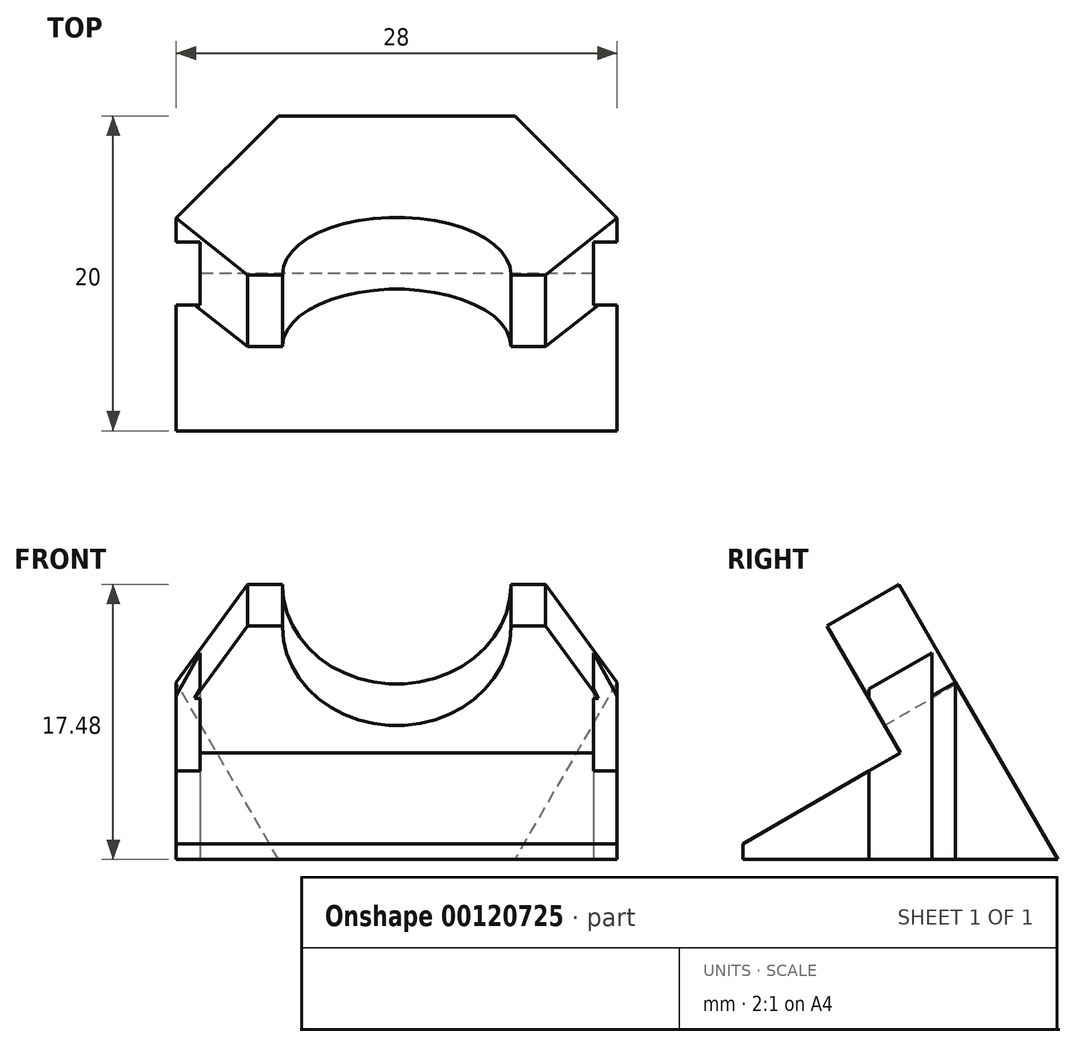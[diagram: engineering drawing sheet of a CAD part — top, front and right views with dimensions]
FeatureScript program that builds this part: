
annotation { "Feature Type Name" : "Feature", "Feature Type Description" : "" }
export const myFeature = defineFeature(function(context is Context, id is Id, definition is map)
    precondition{}
    {
        {
            var Q0;
            Q0=qCreatedBy(makeId("Top.planeOp"),FACE);
            var sketch = newSketch(context, id + "F0", { "sketchPlane" : qUnion([Q0])});
            skLineSegment(sketch, "E0.bottom", {"start": v(-14, 10) * mm, "end": v(14, 10) * mm});
            skLineSegment(sketch, "E0.top", {"start": v(-14, -10) * mm, "end": v(14, -10) * mm});
            skLineSegment(sketch, "E0.left", {"start": v(-14, 10) * mm, "end": v(-14, -10) * mm});
            skLineSegment(sketch, "E0.right", {"start": v(14, 10) * mm, "end": v(14, -10) * mm});
            skSolve(sketch);
        }
        {
            var Q0;
            Q0=makeQuery(id+"F0.imprint","IMPRINT",FACE,{"disambiguationData":[TD([[makeQuery(id+"F0.imprint","IMPRINT",EDGE,{"derivedFrom":sQuery(id+"F0.wireOp",EDGE,"E0.bottom")}),-1.0]])]});
            extrude(context, id + "F1", {"entities" : qUnion([Q0]), "depth" : 20 * mm});
        }
        {
            var Q0;
            Q0=qCreatedBy(makeId("Top.planeOp"),FACE);
            var sketch = newSketch(context, id + "F2", { "sketchPlane" : qUnion([Q0])});
            skLineSegment(sketch, "E1", {"start": v(-7.5, 10) * mm, "end": v(-14, 3.5) * mm});
            skLineSegment(sketch, "E2", {"start": v(-14, 3.5) * mm, "end": v(-14, 10) * mm});
            skLineSegment(sketch, "E3", {"start": v(-14, 10) * mm, "end": v(-7.5, 10) * mm});
            skSolve(sketch);
        }
        {
            var Q0;
            Q0 = qSketchRegion(id + "F2", true);
            extrude(context, id + "F3", {"entities" : qUnion([Q0]), "depth" : 20 * mm});
        }
        {
            var Q0;
            Q0=makeQuery(id+"F3.opExtrude","SWEPT_BODY",BODY,{"disambiguationData":[OSD([sQuery(id+"F2.wireOp",EDGE,"E1"),sQuery(id+"F2.wireOp",EDGE,"E2"),sQuery(id+"F2.wireOp",EDGE,"E3")])]});
            var Q1;
            Q1=qCreatedBy(makeId("Right.planeOp"),FACE);
            mirror(context, id + "F4", {"entities" : qUnion([Q0]), "mirrorPlane" : qUnion([Q1])});
        }
        {
            var Q0;
            Q0=qCreatedBy(makeId("Right.planeOp"),FACE);
            var sketch = newSketch(context, id + "F5", { "sketchPlane" : qUnion([Q0])});
            skLineSegment(sketch, "E4", {"start": v(10, 0) * mm, "end": v(10, 25.53) * mm});
            skLineSegment(sketch, "E5", {"start": v(10, 25.53) * mm, "end": v(-4.74, 25.53) * mm});
            skLineSegment(sketch, "E6", {"start": v(-4.74, 25.53) * mm, "end": v(10, 0) * mm});
            skSolve(sketch);
        }
        {
            var Q0;
            Q0 = qSketchRegion(id + "F5", true);
            extrude(context, id + "F6", {"entities" : qUnion([Q0]), "endBound" : BoundingType.SYMMETRIC, "depth" : 35 * mm});
        }
        {
            var Q0;
            Q0=qCreatedBy(makeId("Top.planeOp"),FACE);
            var sketch = newSketch(context, id + "F7", { "sketchPlane" : qUnion([Q0])});
            skLineSegment(sketch, "E7.bottom", {"start": v(-14, -2) * mm, "end": v(-12.5, -2) * mm});
            skLineSegment(sketch, "E7.top", {"start": v(-14, 2) * mm, "end": v(-12.5, 2) * mm});
            skLineSegment(sketch, "E7.left", {"start": v(-14, -2) * mm, "end": v(-14, 2) * mm});
            skLineSegment(sketch, "E7.right", {"start": v(-12.5, -2) * mm, "end": v(-12.5, 2) * mm});
            skSolve(sketch);
        }
        {
            var Q0;
            Q0 = qSketchRegion(id + "F7", true);
            extrude(context, id + "F8", {"entities" : qUnion([Q0]), "depth" : 40 * mm});
        }
        {
            var Q0;
            Q0=makeQuery(id+"F8.opExtrude","SWEPT_BODY",BODY,{"disambiguationData":[OSD([sQuery(id+"F7.wireOp",EDGE,"E7.bottom"),sQuery(id+"F7.wireOp",EDGE,"E7.top"),sQuery(id+"F7.wireOp",EDGE,"E7.left"),sQuery(id+"F7.wireOp",EDGE,"E7.right")])]});
            var Q1;
            Q1=qCreatedBy(makeId("Right.planeOp"),FACE);
            mirror(context, id + "F9", {"entities" : qUnion([Q0]), "mirrorPlane" : qUnion([Q1])});
        }
        {
            var Q0;
            Q0=makeQuery(id+"F3.opExtrude","SWEPT_BODY",BODY,{"disambiguationData":[OSD([sQuery(id+"F2.wireOp",EDGE,"E1"),sQuery(id+"F2.wireOp",EDGE,"E2"),sQuery(id+"F2.wireOp",EDGE,"E3")])]});
            var Q1;
            Q1=makeQuery(id+"F4.opPattern","COPY",BODY,{"derivedFrom":makeQuery(id+"F3.opExtrude","SWEPT_BODY",BODY,{"disambiguationData":[OSD([sQuery(id+"F2.wireOp",EDGE,"E1"),sQuery(id+"F2.wireOp",EDGE,"E2"),sQuery(id+"F2.wireOp",EDGE,"E3")])]}),"instanceName":"1"});
            var Q2;
            Q2=makeQuery(id+"F6.opExtrude","SWEPT_BODY",BODY,{"disambiguationData":[OSD([sQuery(id+"F5.wireOp",EDGE,"E4"),sQuery(id+"F5.wireOp",EDGE,"E5"),sQuery(id+"F5.wireOp",EDGE,"E6")])]});
            var Q3;
            Q3=makeQuery(id+"F8.opExtrude","SWEPT_BODY",BODY,{"disambiguationData":[OSD([sQuery(id+"F7.wireOp",EDGE,"E7.bottom"),sQuery(id+"F7.wireOp",EDGE,"E7.top"),sQuery(id+"F7.wireOp",EDGE,"E7.left"),sQuery(id+"F7.wireOp",EDGE,"E7.right")])]});
            var Q4;
            Q4=makeQuery(id+"F9.opPattern","COPY",BODY,{"derivedFrom":makeQuery(id+"F8.opExtrude","SWEPT_BODY",BODY,{"disambiguationData":[OSD([sQuery(id+"F7.wireOp",EDGE,"E7.bottom"),sQuery(id+"F7.wireOp",EDGE,"E7.top"),sQuery(id+"F7.wireOp",EDGE,"E7.left"),sQuery(id+"F7.wireOp",EDGE,"E7.right")])]}),"instanceName":"1"});
            var Q5;
            Q5=makeQuery(id+"F1.opExtrude","SWEPT_BODY",BODY,{"disambiguationData":[OSD([sQuery(id+"F0.wireOp",EDGE,"E0.bottom"),sQuery(id+"F0.wireOp",EDGE,"E0.top"),sQuery(id+"F0.wireOp",EDGE,"E0.left"),sQuery(id+"F0.wireOp",EDGE,"E0.right")])]});
            booleanBodies(context, id + "F10", {"operationType" : BooleanOperationType.SUBTRACTION, "tools" : qUnion([Q0, Q1, Q2, Q3, Q4]), "targets" : qUnion([Q5])});
        }
        {
            var Q0;
            Q0=qCreatedBy(makeId("Right.planeOp"),FACE);
            var sketch = newSketch(context, id + "F11", { "sketchPlane" : qUnion([Q0])});
            skLineSegment(sketch, "E8", {"start": v(-10, 1) * mm, "end": v(0, 6.77) * mm});
            skLineSegment(sketch, "E9", {"start": v(0, 6.77) * mm, "end": v(-10, 24.1) * mm});
            skLineSegment(sketch, "E10", {"start": v(-10, 24.1) * mm, "end": v(-10, 1) * mm});
            skSolve(sketch);
        }
        {
            var Q0;
            Q0=makeQuery(id+"F11.imprint","IMPRINT",FACE,{"disambiguationData":[TD([[makeQuery(id+"F11.imprint","IMPRINT",EDGE,{"derivedFrom":sQuery(id+"F11.wireOp",EDGE,"E8")}),1.0]])]});
            extrude(context, id + "F12", {"entities" : qUnion([Q0]), "endBound" : BoundingType.SYMMETRIC, "depth" : 30 * mm});
        }
        {
            var Q0;
            Q0=makeQuery(id+"F12.opExtrude","SWEPT_BODY",BODY,{"disambiguationData":[OSD([sQuery(id+"F11.wireOp",EDGE,"E8"),sQuery(id+"F11.wireOp",EDGE,"E9"),sQuery(id+"F11.wireOp",EDGE,"E10")])]});
            var Q1;
            Q1=makeQuery(id+"F1.opExtrude","SWEPT_BODY",BODY,{"disambiguationData":[OSD([sQuery(id+"F0.wireOp",EDGE,"E0.bottom"),sQuery(id+"F0.wireOp",EDGE,"E0.top"),sQuery(id+"F0.wireOp",EDGE,"E0.left"),sQuery(id+"F0.wireOp",EDGE,"E0.right")])]});
            booleanBodies(context, id + "F13", {"operationType" : BooleanOperationType.SUBTRACTION, "tools" : qUnion([Q0]), "targets" : qUnion([Q1])});
        }
        {
            var Q0;
            Q0=makeQuery(id+"F13.opBoolean","COPY",FACE,{"derivedFrom":makeQuery(id+"F12.opExtrude","SWEPT_FACE",FACE,{"disambiguationData":[OSD([sQuery(id+"F11.wireOp",EDGE,"E9")])]})});
            var sketch = newSketch(context, id + "F14", { "sketchPlane" : qUnion([Q0])});
            skLineSegment(sketch, "E11.bottom", {"start": v(0, 5.87) * mm, "end": v(9.74, 5.87) * mm});
            skLineSegment(sketch, "E11.top", {"start": v(0, 15.12) * mm, "end": v(9.74, 15.12) * mm});
            skLineSegment(sketch, "E11.left", {"start": v(0, 5.87) * mm, "end": v(0, 15.12) * mm});
            skLineSegment(sketch, "E11.right", {"start": v(9.74, 5.87) * mm, "end": v(9.74, 15.12) * mm});
            skSolve(sketch);
        }
        {
            var Q0;
            Q0=sQuery(id+"F14.wireOp",VERTEX,"E11.left.end");
            var Q1;
            Q1=makeQuery(id+"F1.opExtrude","SWEPT_BODY",BODY,{"disambiguationData":[OSD([sQuery(id+"F0.wireOp",EDGE,"E0.bottom"),sQuery(id+"F0.wireOp",EDGE,"E0.top"),sQuery(id+"F0.wireOp",EDGE,"E0.left"),sQuery(id+"F0.wireOp",EDGE,"E0.right")])]});
            hole(context, id + "F15", {"style" : HoleStyle.SIMPLE, "endStyle" : HoleEndStyle.THROUGH, "holeDiameter" : 14.5 * mm, "locations" : qUnion([Q0]), "scope" : qUnion([Q1]), "isTappedThrough" : true});
        }
        {
            var Q0;
            Q0=qCreatedBy(makeId("Right.planeOp"),FACE);
            var sketch = newSketch(context, id + "F16", { "sketchPlane" : qUnion([Q0])});
            skLineSegment(sketch, "E12", {"start": v(6, 21) * mm, "end": v(-7.5, 13.2) * mm});
            skLineSegment(sketch, "E13", {"start": v(-7.5, 13.2) * mm, "end": v(-12, 21) * mm});
            skLineSegment(sketch, "E14", {"start": v(-12, 21) * mm, "end": v(6, 21) * mm});
            skSolve(sketch);
        }
        {
            var Q0;
            Q0 = qSketchRegion(id + "F16", true);
            extrude(context, id + "F17", {"entities" : qUnion([Q0]), "endBound" : BoundingType.SYMMETRIC, "depth" : 40 * mm});
        }
        {
            var Q0;
            Q0=makeQuery(id+"F10.opBoolean","COPY",FACE,{"derivedFrom":makeQuery(id+"F6.opExtrude","SWEPT_FACE",FACE,{"disambiguationData":[OSD([sQuery(id+"F5.wireOp",EDGE,"E6")])]})});
            var sketch = newSketch(context, id + "F18", { "sketchPlane" : qUnion([Q0])});
            skLineSegment(sketch, "E15", {"start": v(8, 17.5) * mm, "end": v(14, 8) * mm});
            skLineSegment(sketch, "E16", {"start": v(14, 8) * mm, "end": v(14, 17.5) * mm});
            skLineSegment(sketch, "E17", {"start": v(14, 17.5) * mm, "end": v(8, 17.5) * mm});
            skSolve(sketch);
        }
        {
            var Q0;
            Q0 = qSketchRegion(id + "F18", true);
            extrude(context, id + "F19", {"entities" : qUnion([Q0]), "endBound" : BoundingType.SYMMETRIC, "depth" : 25 * mm});
        }
        {
            var Q0;
            Q0=makeQuery(id+"F19.opExtrude","SWEPT_BODY",BODY,{"disambiguationData":[OSD([sQuery(id+"F18.wireOp",EDGE,"E15"),sQuery(id+"F18.wireOp",EDGE,"E16"),sQuery(id+"F18.wireOp",EDGE,"E17")])]});
            var Q1;
            Q1=qCreatedBy(makeId("Right.planeOp"),FACE);
            mirror(context, id + "F20", {"entities" : qUnion([Q0]), "mirrorPlane" : qUnion([Q1])});
        }
        {
            var Q0;
            Q0=makeQuery(id+"F20.opPattern","COPY",BODY,{"derivedFrom":makeQuery(id+"F19.opExtrude","SWEPT_BODY",BODY,{"disambiguationData":[OSD([sQuery(id+"F18.wireOp",EDGE,"E15"),sQuery(id+"F18.wireOp",EDGE,"E16"),sQuery(id+"F18.wireOp",EDGE,"E17")])]}),"instanceName":"1"});
            var Q1;
            Q1=makeQuery(id+"F19.opExtrude","SWEPT_BODY",BODY,{"disambiguationData":[OSD([sQuery(id+"F18.wireOp",EDGE,"E15"),sQuery(id+"F18.wireOp",EDGE,"E16"),sQuery(id+"F18.wireOp",EDGE,"E17")])]});
            var Q2;
            Q2=makeQuery(id+"F17.opExtrude","SWEPT_BODY",BODY,{"disambiguationData":[OSD([sQuery(id+"F16.wireOp",EDGE,"E12"),sQuery(id+"F16.wireOp",EDGE,"E13"),sQuery(id+"F16.wireOp",EDGE,"E14")])]});
            var Q3;
            Q3=makeQuery(id+"F1.opExtrude","SWEPT_BODY",BODY,{"disambiguationData":[OSD([sQuery(id+"F0.wireOp",EDGE,"E0.bottom"),sQuery(id+"F0.wireOp",EDGE,"E0.top"),sQuery(id+"F0.wireOp",EDGE,"E0.left"),sQuery(id+"F0.wireOp",EDGE,"E0.right")])]});
            booleanBodies(context, id + "F21", {"operationType" : BooleanOperationType.SUBTRACTION, "tools" : qUnion([Q0, Q1, Q2]), "targets" : qUnion([Q3])});
        }
    });
